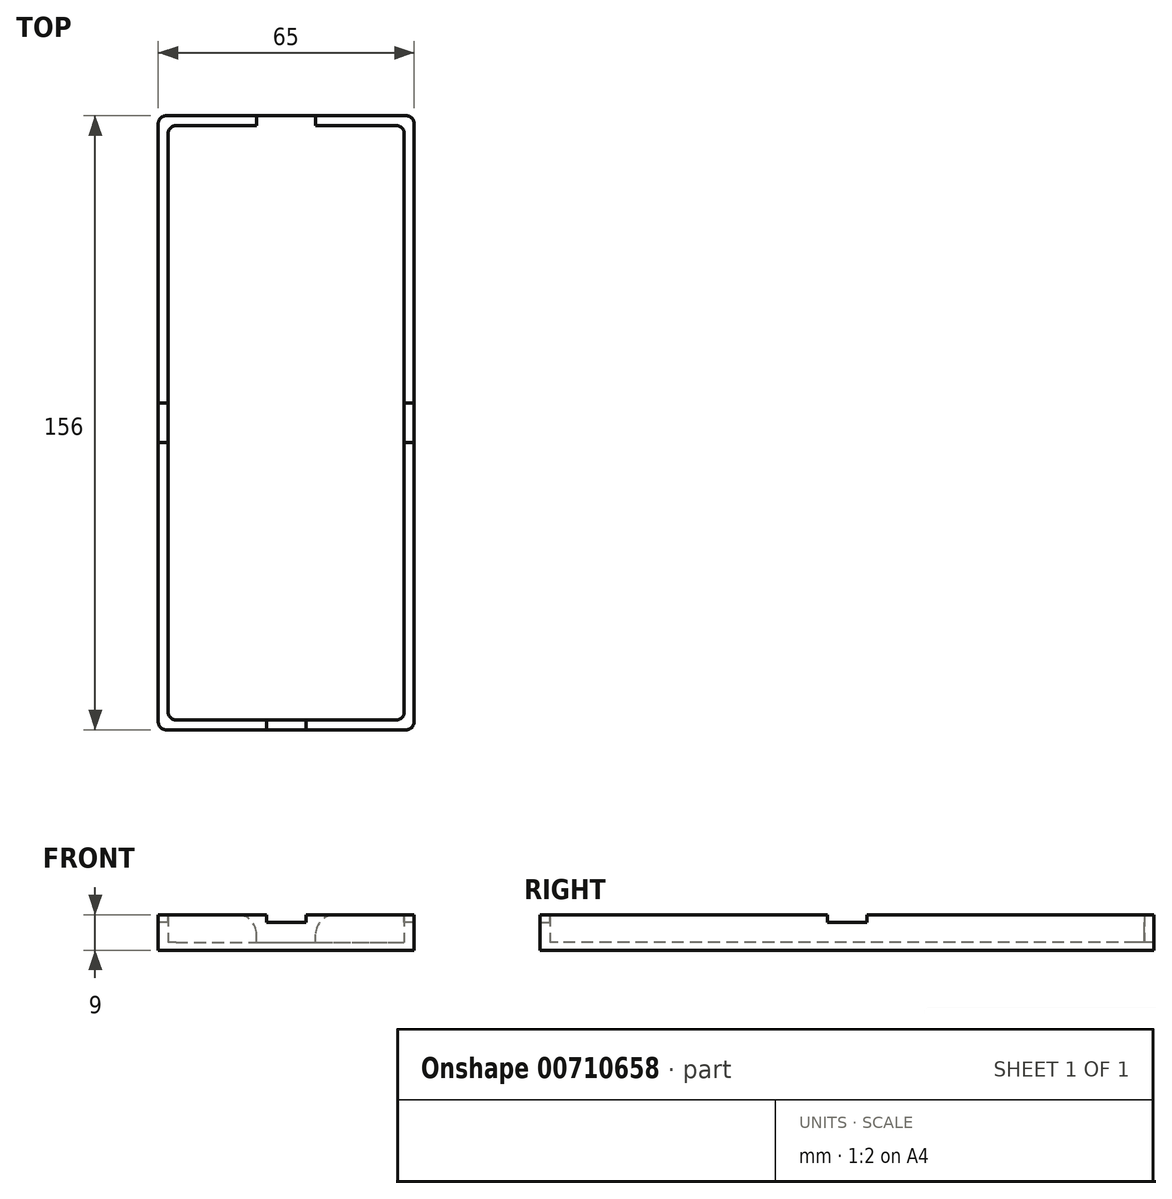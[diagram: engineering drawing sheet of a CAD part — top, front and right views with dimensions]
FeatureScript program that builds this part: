
annotation { "Feature Type Name" : "Feature", "Feature Type Description" : "" }
export const myFeature = defineFeature(function(context is Context, id is Id, definition is map)
    precondition{}
    {
        {
            var Q0;
            Q0=qCreatedBy(makeId("Top.planeOp"),FACE);
            var sketch = newSketch(context, id + "F0", { "sketchPlane" : qUnion([Q0])});
            skLineSegment(sketch, "E0.bottom", {"start": v(30, -75.5) * mm, "end": v(-30, -75.5) * mm});
            skLineSegment(sketch, "E0.top", {"start": v(30, 75.5) * mm, "end": v(-30, 75.5) * mm});
            skLineSegment(sketch, "E0.left", {"start": v(30, -75.5) * mm, "end": v(30, 75.5) * mm});
            skLineSegment(sketch, "E0.right", {"start": v(-30, -75.5) * mm, "end": v(-30, 75.5) * mm});
            skPoint(sketch, "E0.middle", {"position": v(0, 0) * mm});
            skLineSegment(sketch, "E1.0", {"start": v(32.5, 78) * mm, "end": v(-32.5, 78) * mm});
            skLineSegment(sketch, "E1.1", {"start": v(32.5, -78) * mm, "end": v(32.5, 78) * mm});
            skLineSegment(sketch, "E1.2", {"start": v(32.5, -78) * mm, "end": v(-32.5, -78) * mm});
            skLineSegment(sketch, "E1.3", {"start": v(-32.5, -78) * mm, "end": v(-32.5, 78) * mm});
            skSolve(sketch);
        }
        {
            var Q0;
            Q0 = qSketchRegion(id + "F0", true);
            var Q1;
            Q1=makeQuery(id+"F0.imprint","IMPRINT",FACE,{"disambiguationData":[TD([[makeQuery(id+"F0.imprint","IMPRINT",EDGE,{"derivedFrom":sQuery(id+"F0.wireOp",EDGE,"E0.bottom")}),-1.0]])]});
            extrude(context, id + "F1", {"entities" : qUnion([Q0, Q1]), "depth" : 2 * mm, "offsetDistance" : 25 * mm});
        }
        {
            var Q0;
            Q0=makeQuery(id+"F0.imprint","IMPRINT",FACE,{"disambiguationData":[TD([[makeQuery(id+"F0.imprint","IMPRINT",EDGE,{"derivedFrom":sQuery(id+"F0.wireOp",EDGE,"E0.bottom")}),1.0]])]});
            extrude(context, id + "F2", {"entities" : qUnion([Q0]), "operationType" : NewBodyOperationType.ADD, "depth" : 7 * mm, "offsetDistance" : 25 * mm});
        }
        {
            var Q0;
            Q0=makeQuery(id+"F2.opExtrude","CAP_FACE",FACE,{"disambiguationData":[OSD([sQuery(id+"F0.wireOp",EDGE,"E0.bottom"),sQuery(id+"F0.wireOp",EDGE,"E0.top"),sQuery(id+"F0.wireOp",EDGE,"E0.left"),sQuery(id+"F0.wireOp",EDGE,"E0.right"),sQuery(id+"F0.wireOp",EDGE,"E1.0"),sQuery(id+"F0.wireOp",EDGE,"E1.1"),sQuery(id+"F0.wireOp",EDGE,"E1.2"),sQuery(id+"F0.wireOp",EDGE,"E1.3")])],"isStart":false});
            var sketch = newSketch(context, id + "F3", { "sketchPlane" : qUnion([Q0])});
            skLineSegment(sketch, "E2", {"start": v(0, 78) * mm, "end": v(0, 75.5) * mm});
            skLineSegment(sketch, "E3.bottom", {"start": v(10, 75.5) * mm, "end": v(-10, 75.5) * mm});
            skLineSegment(sketch, "E3.top", {"start": v(10, 78) * mm, "end": v(-10, 78) * mm});
            skLineSegment(sketch, "E3.left", {"start": v(10, 75.5) * mm, "end": v(10, 78) * mm});
            skLineSegment(sketch, "E3.right", {"start": v(-10, 75.5) * mm, "end": v(-10, 78) * mm});
            skPoint(sketch, "E3.middle", {"position": v(0, 76.75) * mm});
            skSolve(sketch);
        }
        {
            var Q0;
            Q0 = qSketchRegion(id + "F3", true);
            var Q1;
            Q1=makeQuery(id+"F1.opExtrude","CAP_FACE",FACE,{"disambiguationData":[OSD([sQuery(id+"F0.wireOp",EDGE,"E1.0"),sQuery(id+"F0.wireOp",EDGE,"E1.1"),sQuery(id+"F0.wireOp",EDGE,"E1.2"),sQuery(id+"F0.wireOp",EDGE,"E1.3")])],"isStart":false});
            extrude(context, id + "F4", {"entities" : qUnion([Q0]), "operationType" : NewBodyOperationType.REMOVE, "endBound" : BoundingType.UP_TO_SURFACE, "oppositeDirection" : true, "depth" : 25 * mm, "endBoundEntityFace" : qUnion([Q1]), "offsetDistance" : 25 * mm});
        }
        {
            var Q0;
            Q0=makeQuery(id+"F2.opExtrude","CAP_FACE",FACE,{"disambiguationData":[OSD([sQuery(id+"F0.wireOp",EDGE,"E0.bottom"),sQuery(id+"F0.wireOp",EDGE,"E0.top"),sQuery(id+"F0.wireOp",EDGE,"E0.left"),sQuery(id+"F0.wireOp",EDGE,"E0.right"),sQuery(id+"F0.wireOp",EDGE,"E1.0"),sQuery(id+"F0.wireOp",EDGE,"E1.1"),sQuery(id+"F0.wireOp",EDGE,"E1.2"),sQuery(id+"F0.wireOp",EDGE,"E1.3")])],"isStart":false});
            extrude(context, id + "F5", {"entities" : qUnion([Q0]), "operationType" : NewBodyOperationType.ADD, "depth" : 2 * mm, "offsetDistance" : 25 * mm});
        }
        {
            var Q0;
            {var subQ0=sQuery(id+"F0.wireOp",EDGE,"E1.3");var subQ1=sQuery(id+"F0.wireOp",EDGE,"E1.0");Q0=makeQuery(id+"F5.boolean.opBoolean","MERGE",EDGE,{"derivedFrom":[makeQuery(id+"F2.boolean.opBoolean","MERGE",EDGE,{"derivedFrom":[makeQuery(id+"F1.opExtrude","SWEPT_EDGE",EDGE,{"disambiguationData":[OSD([subQ1,subQ0])]}),makeQuery(id+"F2.opExtrude","SWEPT_EDGE",EDGE,{"disambiguationData":[OSD([subQ1,subQ0])]})]}),makeQuery(id+"F5.opExtrude","SWEPT_EDGE",EDGE,{"disambiguationData":[OSD([subQ1,subQ0])]})]});}
            var Q1;
            {var subQ0=sQuery(id+"F0.wireOp",EDGE,"E1.1");var subQ1=sQuery(id+"F0.wireOp",EDGE,"E1.0");Q1=makeQuery(id+"F5.boolean.opBoolean","MERGE",EDGE,{"derivedFrom":[makeQuery(id+"F2.boolean.opBoolean","MERGE",EDGE,{"derivedFrom":[makeQuery(id+"F1.opExtrude","SWEPT_EDGE",EDGE,{"disambiguationData":[OSD([subQ1,subQ0])]}),makeQuery(id+"F2.opExtrude","SWEPT_EDGE",EDGE,{"disambiguationData":[OSD([subQ1,subQ0])]})]}),makeQuery(id+"F5.opExtrude","SWEPT_EDGE",EDGE,{"disambiguationData":[OSD([subQ1,subQ0])]})]});}
            var Q2;
            {var subQ0=sQuery(id+"F0.wireOp",EDGE,"E1.2");var subQ1=sQuery(id+"F0.wireOp",EDGE,"E1.1");Q2=makeQuery(id+"F5.boolean.opBoolean","MERGE",EDGE,{"derivedFrom":[makeQuery(id+"F2.boolean.opBoolean","MERGE",EDGE,{"derivedFrom":[makeQuery(id+"F1.opExtrude","SWEPT_EDGE",EDGE,{"disambiguationData":[OSD([subQ1,subQ0])]}),makeQuery(id+"F2.opExtrude","SWEPT_EDGE",EDGE,{"disambiguationData":[OSD([subQ1,subQ0])]})]}),makeQuery(id+"F5.opExtrude","SWEPT_EDGE",EDGE,{"disambiguationData":[OSD([subQ1,subQ0])]})]});}
            var Q3;
            {var subQ0=sQuery(id+"F0.wireOp",EDGE,"E1.3");var subQ1=sQuery(id+"F0.wireOp",EDGE,"E1.2");Q3=makeQuery(id+"F5.boolean.opBoolean","MERGE",EDGE,{"derivedFrom":[makeQuery(id+"F2.boolean.opBoolean","MERGE",EDGE,{"derivedFrom":[makeQuery(id+"F1.opExtrude","SWEPT_EDGE",EDGE,{"disambiguationData":[OSD([subQ1,subQ0])]}),makeQuery(id+"F2.opExtrude","SWEPT_EDGE",EDGE,{"disambiguationData":[OSD([subQ1,subQ0])]})]}),makeQuery(id+"F5.opExtrude","SWEPT_EDGE",EDGE,{"disambiguationData":[OSD([subQ1,subQ0])]})]});}
            fillet(context, id + "F6", {"entities" : qUnion([Q0, Q1, Q2, Q3]), "radius" : 2 * mm, "tangentPropagation" : true, "allowEdgeOverflow" : false});
        }
        {
            var Q0;
            {var subQ0=sQuery(id+"F0.wireOp",EDGE,"E0.right");var subQ1=sQuery(id+"F0.wireOp",EDGE,"E0.top");Q0=makeQuery(id+"F5.boolean.opBoolean","MERGE",EDGE,{"derivedFrom":[makeQuery(id+"F2.opExtrude","SWEPT_EDGE",EDGE,{"disambiguationData":[OSD([subQ1,subQ0])]}),makeQuery(id+"F5.opExtrude","SWEPT_EDGE",EDGE,{"disambiguationData":[OSD([subQ1,subQ0])]})]});}
            var Q1;
            {var subQ0=sQuery(id+"F0.wireOp",EDGE,"E0.left");var subQ1=sQuery(id+"F0.wireOp",EDGE,"E0.top");Q1=makeQuery(id+"F5.boolean.opBoolean","MERGE",EDGE,{"derivedFrom":[makeQuery(id+"F2.opExtrude","SWEPT_EDGE",EDGE,{"disambiguationData":[OSD([subQ1,subQ0])]}),makeQuery(id+"F5.opExtrude","SWEPT_EDGE",EDGE,{"disambiguationData":[OSD([subQ1,subQ0])]})]});}
            var Q2;
            {var subQ0=sQuery(id+"F0.wireOp",EDGE,"E0.left");var subQ1=sQuery(id+"F0.wireOp",EDGE,"E0.bottom");Q2=makeQuery(id+"F5.boolean.opBoolean","MERGE",EDGE,{"derivedFrom":[makeQuery(id+"F2.opExtrude","SWEPT_EDGE",EDGE,{"disambiguationData":[OSD([subQ1,subQ0])]}),makeQuery(id+"F5.opExtrude","SWEPT_EDGE",EDGE,{"disambiguationData":[OSD([subQ1,subQ0])]})]});}
            var Q3;
            {var subQ0=sQuery(id+"F0.wireOp",EDGE,"E0.right");var subQ1=sQuery(id+"F0.wireOp",EDGE,"E0.bottom");Q3=makeQuery(id+"F5.boolean.opBoolean","MERGE",EDGE,{"derivedFrom":[makeQuery(id+"F2.opExtrude","SWEPT_EDGE",EDGE,{"disambiguationData":[OSD([subQ1,subQ0])]}),makeQuery(id+"F5.opExtrude","SWEPT_EDGE",EDGE,{"disambiguationData":[OSD([subQ1,subQ0])]})]});}
            fillet(context, id + "F7", {"entities" : qUnion([Q0, Q1, Q2, Q3]), "radius" : 2 * mm, "tangentPropagation" : true, "allowEdgeOverflow" : false});
        }
        {
            var Q0;
            Q0=makeQuery(id+"F5.opExtrude","CAP_FACE",FACE,{"disambiguationData":[OSD([sQuery(id+"F0.wireOp",EDGE,"E0.bottom"),sQuery(id+"F0.wireOp",EDGE,"E0.top"),sQuery(id+"F0.wireOp",EDGE,"E0.left"),sQuery(id+"F0.wireOp",EDGE,"E0.right"),sQuery(id+"F0.wireOp",EDGE,"E1.0"),sQuery(id+"F0.wireOp",EDGE,"E1.1"),sQuery(id+"F0.wireOp",EDGE,"E1.2"),sQuery(id+"F0.wireOp",EDGE,"E1.3")])],"isStart":false});
            var sketch = newSketch(context, id + "F8", { "sketchPlane" : qUnion([Q0])});
            skLineSegment(sketch, "E4", {"start": v(0, -75.5) * mm, "end": v(0, -78) * mm});
            skLineSegment(sketch, "E5.bottom", {"start": v(5, -78) * mm, "end": v(-5, -78) * mm});
            skLineSegment(sketch, "E5.top", {"start": v(5, -75.5) * mm, "end": v(-5, -75.5) * mm});
            skLineSegment(sketch, "E5.left", {"start": v(5, -78) * mm, "end": v(5, -75.5) * mm});
            skLineSegment(sketch, "E5.right", {"start": v(-5, -78) * mm, "end": v(-5, -75.5) * mm});
            skPoint(sketch, "E5.middle", {"position": v(0, -76.75) * mm});
            skLineSegment(sketch, "E6", {"start": v(-32.5, 0) * mm, "end": v(-30, 0) * mm});
            skLineSegment(sketch, "E7", {"start": v(30, 0) * mm, "end": v(32.5, 0) * mm});
            skLineSegment(sketch, "E8.bottom", {"start": v(-30, -5) * mm, "end": v(-32.5, -5) * mm});
            skLineSegment(sketch, "E8.top", {"start": v(-30, 5) * mm, "end": v(-32.5, 5) * mm});
            skLineSegment(sketch, "E8.left", {"start": v(-30, -5) * mm, "end": v(-30, 5) * mm});
            skLineSegment(sketch, "E8.right", {"start": v(-32.5, -5) * mm, "end": v(-32.5, 5) * mm});
            skPoint(sketch, "E8.middle", {"position": v(-31.25, 0) * mm});
            skLineSegment(sketch, "E9.bottom", {"start": v(32.5, -5) * mm, "end": v(30, -5) * mm});
            skLineSegment(sketch, "E9.top", {"start": v(32.5, 5) * mm, "end": v(30, 5) * mm});
            skLineSegment(sketch, "E9.left", {"start": v(32.5, -5) * mm, "end": v(32.5, 5) * mm});
            skLineSegment(sketch, "E9.right", {"start": v(30, -5) * mm, "end": v(30, 5) * mm});
            skPoint(sketch, "E9.middle", {"position": v(31.25, 0) * mm});
            skSolve(sketch);
        }
        {
            var Q0;
            Q0 = qSketchRegion(id + "F8", true);
            extrude(context, id + "F9", {"entities" : qUnion([Q0]), "operationType" : NewBodyOperationType.REMOVE, "oppositeDirection" : true, "depth" : 2 * mm, "offsetDistance" : 25 * mm});
        }
        {
            var Q0;
            {var subQ0=sQuery(id+"F3.wireOp",EDGE,"E3.right");Q0=makeQuery(id+"F5.boolean.opBoolean","MERGE",FACE,{"derivedFrom":[makeQuery(id+"F4.boolean.opBoolean","COPY",FACE,{"derivedFrom":makeQuery(id+"F4.opExtrude","SWEPT_FACE",FACE,{"disambiguationData":[OSD([subQ0])]})}),makeQuery(id+"F5.opExtrude","SWEPT_FACE",FACE,{"disambiguationData":[OSD([subQ0])]})]});}
            extrude(context, id + "F10", {"entities" : qUnion([Q0]), "operationType" : NewBodyOperationType.ADD, "depth" : 2.5 * mm, "offsetDistance" : 25 * mm});
        }
        {
            var Q0;
            {var subQ0=sQuery(id+"F3.wireOp",EDGE,"E3.left");Q0=makeQuery(id+"F5.boolean.opBoolean","MERGE",FACE,{"derivedFrom":[makeQuery(id+"F4.boolean.opBoolean","COPY",FACE,{"derivedFrom":makeQuery(id+"F4.opExtrude","SWEPT_FACE",FACE,{"disambiguationData":[OSD([subQ0])]})}),makeQuery(id+"F5.opExtrude","SWEPT_FACE",FACE,{"disambiguationData":[OSD([subQ0])]})]});}
            extrude(context, id + "F11", {"entities" : qUnion([Q0]), "operationType" : NewBodyOperationType.ADD, "depth" : 2.5 * mm, "offsetDistance" : 25 * mm});
        }
        {
            var Q0;
            Q0=makeQuery(id+"F10.opExtrude","CAP_EDGE",EDGE,{"disambiguationData":[OSD([sQuery(id+"F0.wireOp",EDGE,"E1.0"),sQuery(id+"F0.wireOp",EDGE,"E1.1"),sQuery(id+"F0.wireOp",EDGE,"E1.2"),sQuery(id+"F0.wireOp",EDGE,"E1.3"),sQuery(id+"F3.wireOp",EDGE,"E3.right")])],"isStart":false});
            var Q1;
            Q1=makeQuery(id+"F11.opExtrude","CAP_EDGE",EDGE,{"disambiguationData":[OSD([sQuery(id+"F0.wireOp",EDGE,"E1.0"),sQuery(id+"F0.wireOp",EDGE,"E1.1"),sQuery(id+"F0.wireOp",EDGE,"E1.2"),sQuery(id+"F0.wireOp",EDGE,"E1.3"),sQuery(id+"F3.wireOp",EDGE,"E3.left")])],"isStart":false});
            fillet(context, id + "F12", {"entities" : qUnion([Q0, Q1]), "radius" : 5 * mm, "tangentPropagation" : true, "allowEdgeOverflow" : false});
        }
    });
